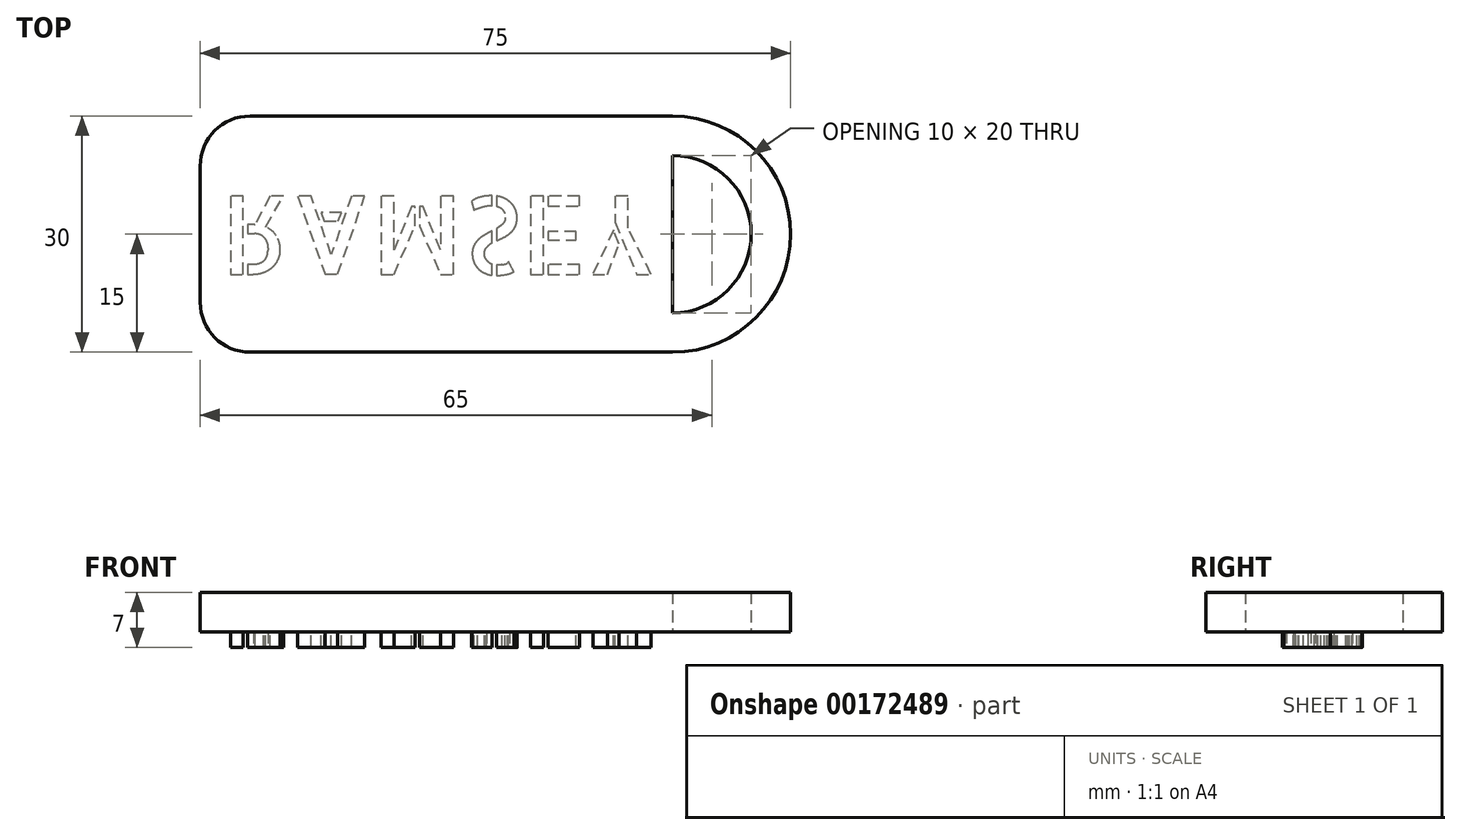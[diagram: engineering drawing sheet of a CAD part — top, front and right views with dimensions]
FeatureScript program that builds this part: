
annotation { "Feature Type Name" : "Feature", "Feature Type Description" : "" }
export const myFeature = defineFeature(function(context is Context, id is Id, definition is map)
    precondition{}
    {
        {
            var Q0;
            Q0=qCreatedBy(makeId("Top.planeOp"),FACE);
            var sketch = newSketch(context, id + "F0", { "sketchPlane" : qUnion([Q0])});
            skLineSegment(sketch, "E0.bottom", {"start": v(-20.72, 5) * mm, "end": v(32.93, 5) * mm});
            skLineSegment(sketch, "E0.top", {"start": v(-20.72, -25) * mm, "end": v(32.93, -25) * mm});
            skLineSegment(sketch, "E0.left", {"start": v(-27.07, -1.35) * mm, "end": v(-27.07, -18.65) * mm});
            skLineSegment(sketch, "E0.right", {"start": v(32.93, 5) * mm, "end": v(32.93, -25) * mm});
            skArc(sketch, "E1", {"start": v(32.93, -25) * mm, "mid": v(47.93, -10) * mm, "end": v(32.93, 5) * mm});
            skArc(sketch, "E2", {"start": v(32.93, -20) * mm, "mid": v(42.93, -10) * mm, "end": v(32.93, 0) * mm});
            skPoint(sketch, "E3.visualSharp", {"position": v(-27.07, 5) * mm});
            skArc(sketch, "E3.filletArc", {"start": v(-20.72, 5) * mm, "mid": v(-25.21, 3.14) * mm, "end": v(-27.07, -1.35) * mm});
            skPoint(sketch, "E4.visualSharp", {"position": v(-27.07, -25) * mm});
            skArc(sketch, "E4.filletArc", {"start": v(-27.07, -18.65) * mm, "mid": v(-25.21, -23.14) * mm, "end": v(-20.72, -25) * mm});
            skSolve(sketch);
        }
        {
            var Q0;
            {var subQ0=sQuery(id+"F0.wireOp",EDGE,"E1");Q0=makeQuery(id+"F0.imprint","IMPRINT",FACE,{"disambiguationData":[TD([[makeQuery(id+"F0.imprint","IMPRINT",EDGE,{"derivedFrom":subQ0}),1.0]])]});}
            var Q1;
            {var subQ2=sQuery(id+"F0.wireOp",EDGE,"E0.bottom");Q1=makeQuery(id+"F0.imprint","IMPRINT",FACE,{"disambiguationData":[TD([[makeQuery(id+"F0.imprint","IMPRINT",EDGE,{"derivedFrom":subQ2}),-1.0]])]});}
            extrude(context, id + "F1", {"entities" : qUnion([Q0, Q1]), "depth" : 5 * mm});
        }
        {
            var Q0;
            Q0=makeQuery(id+"F1.opExtrude","CAP_FACE",FACE,{"disambiguationData":[OSD([sQuery(id+"F0.wireOp",EDGE,"E0.bottom"),sQuery(id+"F0.wireOp",EDGE,"E0.top"),sQuery(id+"F0.wireOp",EDGE,"E0.left"),sQuery(id+"F0.wireOp",EDGE,"E0.right"),sQuery(id+"F0.wireOp",EDGE,"E1"),sQuery(id+"F0.wireOp",EDGE,"E2"),sQuery(id+"F0.wireOp",EDGE,"E3.filletArc"),sQuery(id+"F0.wireOp",EDGE,"E4.filletArc")])],"isStart":true});
            var sketch = newSketch(context, id + "F2", { "sketchPlane" : qUnion([Q0])});
            skText(sketch, "E5", { "text": "RAMSEY", "fontName": "AllertaStencil-Regular.ttf"});
            const initialGuessF2  = {"E5": [-0.02443, 0.00517, 1, 0, 0.00993]};
            skSetInitialGuess(sketch, initialGuessF2);
            skSolve(sketch);
        }
        {
            var Q0;
            Q0 = qSketchRegion(id + "F2", true);
            extrude(context, id + "F3", {"entities" : qUnion([Q0]), "depth" : 2 * mm});
        }
    });
